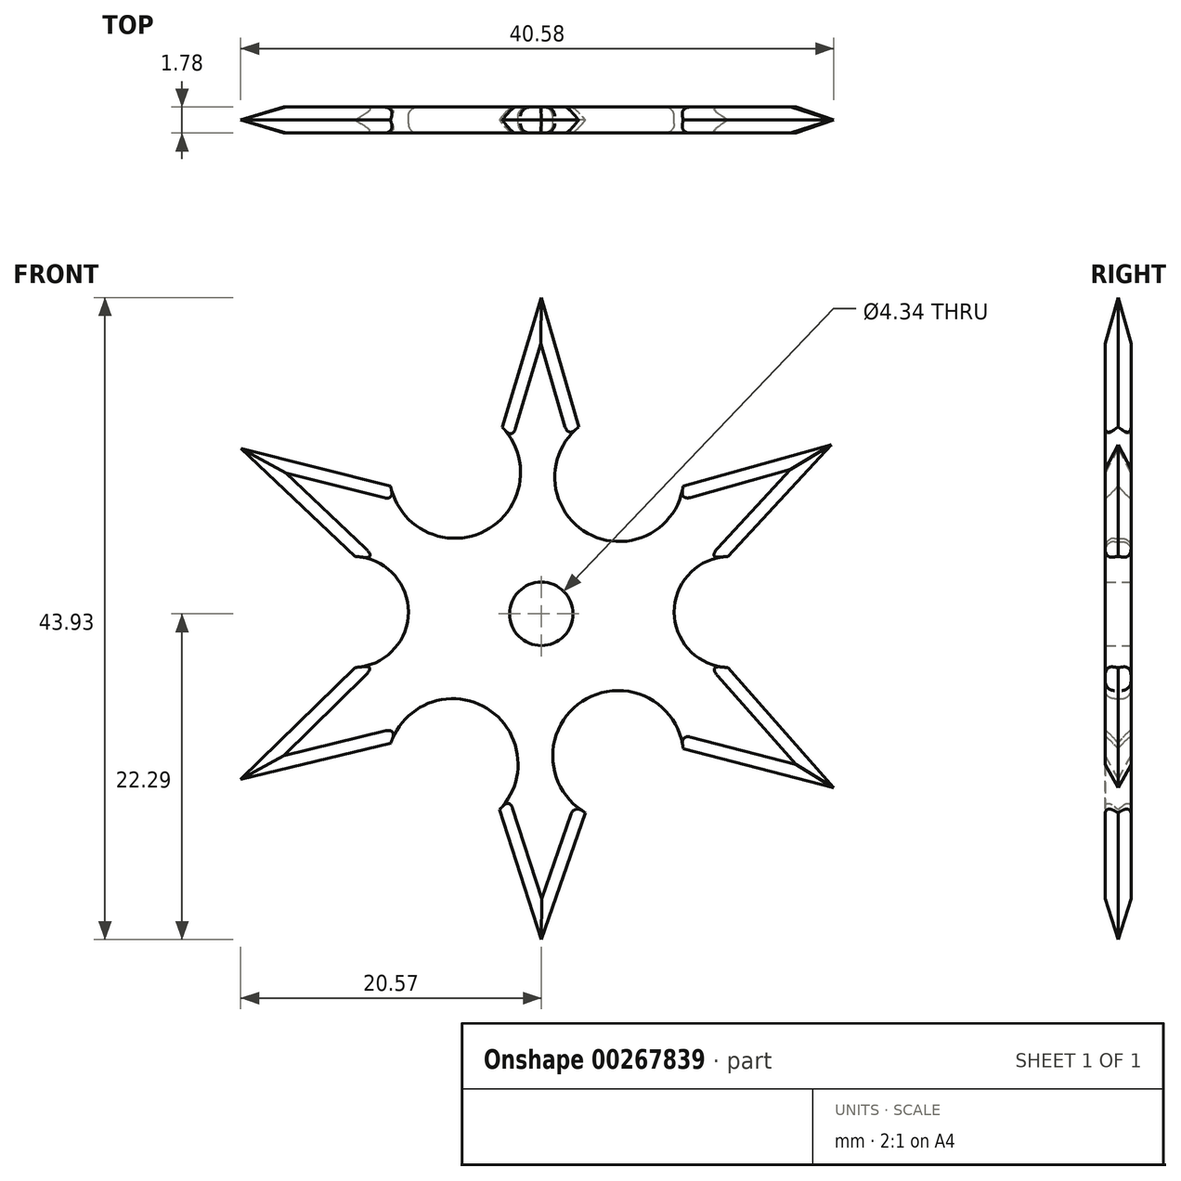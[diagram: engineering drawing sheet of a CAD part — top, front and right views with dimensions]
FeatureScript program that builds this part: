
annotation { "Feature Type Name" : "Feature", "Feature Type Description" : "" }
export const myFeature = defineFeature(function(context is Context, id is Id, definition is map)
    precondition{}
    {
        {
            var Q0;
            Q0=qCreatedBy(makeId("Front.planeOp"),FACE);
            var sketch = newSketch(context, id + "F0", { "sketchPlane" : qUnion([Q0])});
            skCircle(sketch, "E0", {"center": v(0, 0) * mm, "radius": 4.02 * mm});
            skArc(sketch, "E1", {"start": v(-12.92, -3.67) * mm, "mid": v(-9.1, 0.13) * mm, "end": v(-12.92, 3.93) * mm});
            skArc(sketch, "E2", {"start": v(12.92, 3.93) * mm, "mid": v(9.1, 0.13) * mm, "end": v(12.92, -3.67) * mm});
            skPoint(sketch, "E3.startSnap0", {"position": v(-9.1, 0.13) * mm});
            skLineSegment(sketch, "E4", {"start": v(-12.92, -3.67) * mm, "end": v(-20.98, -11.56) * mm});
            skLineSegment(sketch, "E5", {"start": v(-20.98, -11.56) * mm, "end": v(-10.34, -8.98) * mm});
            skLineSegment(sketch, "E6", {"start": v(9.72, -9.35) * mm, "end": v(20.38, -12.12) * mm});
            skLineSegment(sketch, "E7", {"start": v(12.92, -3.67) * mm, "end": v(20.38, -12.12) * mm});
            skLineSegment(sketch, "E8", {"start": v(12.92, 3.93) * mm, "end": v(20.25, 11.82) * mm});
            skLineSegment(sketch, "E9", {"start": v(9.72, 8.88) * mm, "end": v(20.25, 11.82) * mm});
            skLineSegment(sketch, "E10", {"start": v(-12.92, 3.93) * mm, "end": v(-20.98, 11.55) * mm});
            skLineSegment(sketch, "E11", {"start": v(-10.34, 8.88) * mm, "end": v(-20.98, 11.55) * mm});
            skCircle(sketch, "E12", {"center": v(0, 0) * mm, "radius": 2.17 * mm});
            skArc(sketch, "E13", {"start": v(-2.96, -13.5) * mm, "mid": v(-3.73, -6.46) * mm, "end": v(-10.34, -8.98) * mm});
            skArc(sketch, "E14", {"start": v(9.72, -9.35) * mm, "mid": v(2.8, -5.98) * mm, "end": v(3.13, -13.66) * mm});
            skLineSegment(sketch, "E15", {"start": v(-2.96, -13.5) * mm, "end": v(0, -22.69) * mm});
            skLineSegment(sketch, "E16", {"start": v(0, -22.69) * mm, "end": v(3.13, -13.66) * mm});
            skArc(sketch, "E17", {"start": v(-10.34, 8.88) * mm, "mid": v(-3.82, 5.69) * mm, "end": v(-2.77, 12.87) * mm});
            skArc(sketch, "E18", {"start": v(2.66, 12.87) * mm, "mid": v(3.16, 5.52) * mm, "end": v(9.72, 8.88) * mm});
            skLineSegment(sketch, "E19", {"start": v(-2.77, 12.87) * mm, "end": v(0, 22.1) * mm});
            skLineSegment(sketch, "E20", {"start": v(0, 22.1) * mm, "end": v(2.66, 12.87) * mm});
            skLineSegment(sketch, "E21", {"start": v(-2.77, 12.87) * mm, "end": v(2.66, 12.87) * mm});
            skLineSegment(sketch, "E22", {"start": v(-2.96, -13.5) * mm, "end": v(3.13, -13.66) * mm});
            skLineSegment(sketch, "E23", {"start": v(-12.92, -3.67) * mm, "end": v(-10.34, -8.98) * mm});
            skLineSegment(sketch, "E24", {"start": v(-12.92, 3.93) * mm, "end": v(-10.34, 8.88) * mm});
            skLineSegment(sketch, "E25", {"start": v(9.72, 8.88) * mm, "end": v(12.92, 3.93) * mm});
            skLineSegment(sketch, "E26", {"start": v(12.92, -3.67) * mm, "end": v(9.72, -9.35) * mm});
            skPoint(sketch, "E27.endSnap0", {"position": v(-11.63, 6.4) * mm});
            skLineSegment(sketch, "E28", {"start": v(-11.63, 6.4) * mm, "end": v(-20.98, 11.55) * mm});
            skLineSegment(sketch, "E29", {"start": v(0, 22.1) * mm, "end": v(0, 12.87) * mm});
            skLineSegment(sketch, "E30", {"start": v(20.25, 11.82) * mm, "end": v(11.32, 6.4) * mm});
            skLineSegment(sketch, "E31", {"start": v(20.38, -12.12) * mm, "end": v(11.32, -6.51) * mm});
            skLineSegment(sketch, "E32", {"start": v(0, -22.69) * mm, "end": v(0, -13.58) * mm});
            skLineSegment(sketch, "E33", {"start": v(-20.98, -11.56) * mm, "end": v(-11.63, -6.32) * mm});
            skLineSegment(sketch, "E34", {"start": v(-12.92, 3.93) * mm, "end": v(-16.3, 8.98) * mm});
            skLineSegment(sketch, "E35", {"start": v(-16.3, 8.98) * mm, "end": v(-10.34, 8.88) * mm});
            skLineSegment(sketch, "E36", {"start": v(-10.34, -8.98) * mm, "end": v(-16.38, -8.98) * mm});
            skLineSegment(sketch, "E37", {"start": v(-16.38, -8.98) * mm, "end": v(-12.92, -3.67) * mm});
            skLineSegment(sketch, "E38", {"start": v(-2.96, -13.5) * mm, "end": v(0, -18.8) * mm});
            skLineSegment(sketch, "E39", {"start": v(0, -18.8) * mm, "end": v(3.13, -13.66) * mm});
            skLineSegment(sketch, "E40", {"start": v(9.72, -9.35) * mm, "end": v(16.19, -9.53) * mm});
            skLineSegment(sketch, "E41", {"start": v(16.19, -9.53) * mm, "end": v(12.92, -3.67) * mm});
            skLineSegment(sketch, "E42", {"start": v(-2.77, 12.87) * mm, "end": v(0, 17.48) * mm});
            skLineSegment(sketch, "E43", {"start": v(0, 17.48) * mm, "end": v(2.66, 12.87) * mm});
            skPoint(sketch, "E44.endSnap0", {"position": v(15.78, 9.11) * mm});
            skLineSegment(sketch, "E45", {"start": v(9.72, 8.88) * mm, "end": v(15.78, 9.11) * mm});
            skLineSegment(sketch, "E46", {"start": v(15.78, 9.11) * mm, "end": v(12.92, 3.93) * mm});
            skSolve(sketch);
        }
        {
            var Q0;
            Q0=makeQuery(id+"F0.imprint","IMPRINT",FACE,{"disambiguationData":[TD([[makeQuery(id+"F0.imprint","IMPRINT",EDGE,{"derivedFrom":sQuery(id+"F0.wireOp",EDGE,"E0")}),-1.0]])]});
            var Q1;
            Q1=makeQuery(id+"F0.imprint","IMPRINT",FACE,{"disambiguationData":[TD([[makeQuery(id+"F0.imprint","IMPRINT",EDGE,{"derivedFrom":sQuery(id+"F0.wireOp",EDGE,"E0")}),1.0]])]});
            extrude(context, id + "F1", {"entities" : qUnion([Q0, Q1]), "endBound" : BoundingType.SYMMETRIC, "depth" : 1.78 * mm});
        }
        {
            var Q0;
            {var subQ0=sQuery(id+"F0.wireOp",EDGE,"E35");Q0=makeQuery(id+"F0.imprint","IMPRINT",FACE,{"disambiguationData":[TD([[makeQuery(id+"F0.imprint","IMPRINT",EDGE,{"derivedFrom":subQ0}),-1.0]])]});}
            var Q1;
            {var subQ0=sQuery(id+"F0.wireOp",EDGE,"E34");Q1=makeQuery(id+"F0.imprint","IMPRINT",FACE,{"disambiguationData":[TD([[makeQuery(id+"F0.imprint","IMPRINT",EDGE,{"derivedFrom":subQ0}),-1.0]])]});}
            var Q2;
            {var subQ0=sQuery(id+"F0.wireOp",EDGE,"E10");Q2=makeQuery(id+"F0.imprint","IMPRINT",FACE,{"disambiguationData":[TD([[makeQuery(id+"F0.imprint","IMPRINT",EDGE,{"derivedFrom":subQ0}),-1.0]])]});}
            var Q3;
            {var subQ0=sQuery(id+"F0.wireOp",EDGE,"E11");Q3=makeQuery(id+"F0.imprint","IMPRINT",FACE,{"disambiguationData":[TD([[makeQuery(id+"F0.imprint","IMPRINT",EDGE,{"derivedFrom":subQ0}),1.0]])]});}
            var Q4;
            {var subQ0=sQuery(id+"F0.wireOp",EDGE,"E42");Q4=makeQuery(id+"F0.imprint","IMPRINT",FACE,{"disambiguationData":[TD([[makeQuery(id+"F0.imprint","IMPRINT",EDGE,{"derivedFrom":subQ0}),-1.0]])]});}
            var Q5;
            {var subQ0=sQuery(id+"F0.wireOp",EDGE,"E43");Q5=makeQuery(id+"F0.imprint","IMPRINT",FACE,{"disambiguationData":[TD([[makeQuery(id+"F0.imprint","IMPRINT",EDGE,{"derivedFrom":subQ0}),-1.0]])]});}
            var Q6;
            {var subQ0=sQuery(id+"F0.wireOp",EDGE,"E20");Q6=makeQuery(id+"F0.imprint","IMPRINT",FACE,{"disambiguationData":[TD([[makeQuery(id+"F0.imprint","IMPRINT",EDGE,{"derivedFrom":subQ0}),-1.0]])]});}
            var Q7;
            {var subQ0=sQuery(id+"F0.wireOp",EDGE,"E19");Q7=makeQuery(id+"F0.imprint","IMPRINT",FACE,{"disambiguationData":[TD([[makeQuery(id+"F0.imprint","IMPRINT",EDGE,{"derivedFrom":subQ0}),-1.0]])]});}
            var Q8;
            {var subQ0=sQuery(id+"F0.wireOp",EDGE,"E5");Q8=makeQuery(id+"F0.imprint","IMPRINT",FACE,{"disambiguationData":[TD([[makeQuery(id+"F0.imprint","IMPRINT",EDGE,{"derivedFrom":subQ0}),1.0]])]});}
            var Q9;
            {var subQ0=sQuery(id+"F0.wireOp",EDGE,"E4");Q9=makeQuery(id+"F0.imprint","IMPRINT",FACE,{"disambiguationData":[TD([[makeQuery(id+"F0.imprint","IMPRINT",EDGE,{"derivedFrom":subQ0}),1.0]])]});}
            var Q10;
            {var subQ0=sQuery(id+"F0.wireOp",EDGE,"E37");Q10=makeQuery(id+"F0.imprint","IMPRINT",FACE,{"disambiguationData":[TD([[makeQuery(id+"F0.imprint","IMPRINT",EDGE,{"derivedFrom":subQ0}),-1.0]])]});}
            var Q11;
            {var subQ0=sQuery(id+"F0.wireOp",EDGE,"E36");Q11=makeQuery(id+"F0.imprint","IMPRINT",FACE,{"disambiguationData":[TD([[makeQuery(id+"F0.imprint","IMPRINT",EDGE,{"derivedFrom":subQ0}),-1.0]])]});}
            var Q12;
            {var subQ0=sQuery(id+"F0.wireOp",EDGE,"E15");Q12=makeQuery(id+"F0.imprint","IMPRINT",FACE,{"disambiguationData":[TD([[makeQuery(id+"F0.imprint","IMPRINT",EDGE,{"derivedFrom":subQ0}),1.0]])]});}
            var Q13;
            {var subQ0=sQuery(id+"F0.wireOp",EDGE,"E16");Q13=makeQuery(id+"F0.imprint","IMPRINT",FACE,{"disambiguationData":[TD([[makeQuery(id+"F0.imprint","IMPRINT",EDGE,{"derivedFrom":subQ0}),1.0]])]});}
            var Q14;
            {var subQ0=sQuery(id+"F0.wireOp",EDGE,"E39");Q14=makeQuery(id+"F0.imprint","IMPRINT",FACE,{"disambiguationData":[TD([[makeQuery(id+"F0.imprint","IMPRINT",EDGE,{"derivedFrom":subQ0}),1.0]])]});}
            var Q15;
            {var subQ0=sQuery(id+"F0.wireOp",EDGE,"E38");Q15=makeQuery(id+"F0.imprint","IMPRINT",FACE,{"disambiguationData":[TD([[makeQuery(id+"F0.imprint","IMPRINT",EDGE,{"derivedFrom":subQ0}),1.0]])]});}
            var Q16;
            {var subQ0=sQuery(id+"F0.wireOp",EDGE,"E7");Q16=makeQuery(id+"F0.imprint","IMPRINT",FACE,{"disambiguationData":[TD([[makeQuery(id+"F0.imprint","IMPRINT",EDGE,{"derivedFrom":subQ0}),-1.0]])]});}
            var Q17;
            {var subQ0=sQuery(id+"F0.wireOp",EDGE,"E41");Q17=makeQuery(id+"F0.imprint","IMPRINT",FACE,{"disambiguationData":[TD([[makeQuery(id+"F0.imprint","IMPRINT",EDGE,{"derivedFrom":subQ0}),1.0]])]});}
            var Q18;
            {var subQ0=sQuery(id+"F0.wireOp",EDGE,"E40");Q18=makeQuery(id+"F0.imprint","IMPRINT",FACE,{"disambiguationData":[TD([[makeQuery(id+"F0.imprint","IMPRINT",EDGE,{"derivedFrom":subQ0}),1.0]])]});}
            var Q19;
            {var subQ0=sQuery(id+"F0.wireOp",EDGE,"E6");Q19=makeQuery(id+"F0.imprint","IMPRINT",FACE,{"disambiguationData":[TD([[makeQuery(id+"F0.imprint","IMPRINT",EDGE,{"derivedFrom":subQ0}),1.0]])]});}
            var Q20;
            {var subQ0=sQuery(id+"F0.wireOp",EDGE,"E8");Q20=makeQuery(id+"F0.imprint","IMPRINT",FACE,{"disambiguationData":[TD([[makeQuery(id+"F0.imprint","IMPRINT",EDGE,{"derivedFrom":subQ0}),1.0]])]});}
            var Q21;
            {var subQ0=sQuery(id+"F0.wireOp",EDGE,"E9");Q21=makeQuery(id+"F0.imprint","IMPRINT",FACE,{"disambiguationData":[TD([[makeQuery(id+"F0.imprint","IMPRINT",EDGE,{"derivedFrom":subQ0}),-1.0]])]});}
            var Q22;
            {var subQ0=sQuery(id+"F0.wireOp",EDGE,"E45");Q22=makeQuery(id+"F0.imprint","IMPRINT",FACE,{"disambiguationData":[TD([[makeQuery(id+"F0.imprint","IMPRINT",EDGE,{"derivedFrom":subQ0}),-1.0]])]});}
            var Q23;
            {var subQ0=sQuery(id+"F0.wireOp",EDGE,"E46");Q23=makeQuery(id+"F0.imprint","IMPRINT",FACE,{"disambiguationData":[TD([[makeQuery(id+"F0.imprint","IMPRINT",EDGE,{"derivedFrom":subQ0}),-1.0]])]});}
            extrude(context, id + "F2", {"entities" : qUnion([Q0, Q1, Q2, Q3, Q4, Q5, Q6, Q7, Q8, Q9, Q10, Q11, Q12, Q13, Q14, Q15, Q16, Q17, Q18, Q19, Q20, Q21, Q22, Q23]), "operationType" : NewBodyOperationType.ADD, "endBound" : BoundingType.SYMMETRIC, "depth" : 1.78 * mm});
        }
        {
            var Q0;
            Q0=makeQuery(id+"F2.opExtrude","CAP_EDGE",EDGE,{"disambiguationData":[OSD([sQuery(id+"F0.wireOp",EDGE,"E11")])],"isStart":false});
            var Q1;
            Q1=makeQuery(id+"F2.opExtrude","CAP_EDGE",EDGE,{"disambiguationData":[OSD([sQuery(id+"F0.wireOp",EDGE,"E10")])],"isStart":false});
            var Q2;
            Q2=makeQuery(id+"F2.opExtrude","CAP_EDGE",EDGE,{"disambiguationData":[OSD([sQuery(id+"F0.wireOp",EDGE,"E19")])],"isStart":false});
            var Q3;
            Q3=makeQuery(id+"F2.opExtrude","CAP_EDGE",EDGE,{"disambiguationData":[OSD([sQuery(id+"F0.wireOp",EDGE,"E20")])],"isStart":false});
            var Q4;
            Q4=makeQuery(id+"F2.opExtrude","CAP_EDGE",EDGE,{"disambiguationData":[OSD([sQuery(id+"F0.wireOp",EDGE,"E9")])],"isStart":false});
            var Q5;
            Q5=makeQuery(id+"F2.opExtrude","CAP_EDGE",EDGE,{"disambiguationData":[OSD([sQuery(id+"F0.wireOp",EDGE,"E8")])],"isStart":false});
            var Q6;
            Q6=makeQuery(id+"F2.opExtrude","CAP_EDGE",EDGE,{"disambiguationData":[OSD([sQuery(id+"F0.wireOp",EDGE,"E7")])],"isStart":false});
            var Q7;
            Q7=makeQuery(id+"F2.opExtrude","CAP_EDGE",EDGE,{"disambiguationData":[OSD([sQuery(id+"F0.wireOp",EDGE,"E6")])],"isStart":false});
            var Q8;
            Q8=makeQuery(id+"F2.opExtrude","CAP_EDGE",EDGE,{"disambiguationData":[OSD([sQuery(id+"F0.wireOp",EDGE,"E16")])],"isStart":false});
            var Q9;
            Q9=makeQuery(id+"F2.opExtrude","CAP_EDGE",EDGE,{"disambiguationData":[OSD([sQuery(id+"F0.wireOp",EDGE,"E15")])],"isStart":false});
            var Q10;
            Q10=makeQuery(id+"F2.opExtrude","CAP_EDGE",EDGE,{"disambiguationData":[OSD([sQuery(id+"F0.wireOp",EDGE,"E5")])],"isStart":false});
            var Q11;
            Q11=makeQuery(id+"F2.opExtrude","CAP_EDGE",EDGE,{"disambiguationData":[OSD([sQuery(id+"F0.wireOp",EDGE,"E4")])],"isStart":false});
            chamfer(context, id + "F3", {"entities" : qUnion([Q0, Q1, Q2, Q3, Q4, Q5, Q6, Q7, Q8, Q9, Q10, Q11]), "width" : 1.02 * mm, "tangentPropagation" : true});
        }
        {
            var Q0;
            Q0=makeQuery(id+"F1.opExtrude","CAP_EDGE",EDGE,{"disambiguationData":[OSD([sQuery(id+"F0.wireOp",EDGE,"E13")])],"isStart":false});
            var Q1;
            Q1=makeQuery(id+"F1.opExtrude","CAP_EDGE",EDGE,{"disambiguationData":[OSD([sQuery(id+"F0.wireOp",EDGE,"E14")])],"isStart":false});
            var Q2;
            Q2=makeQuery(id+"F1.opExtrude","CAP_EDGE",EDGE,{"disambiguationData":[OSD([sQuery(id+"F0.wireOp",EDGE,"E2")])],"isStart":false});
            var Q3;
            Q3=makeQuery(id+"F1.opExtrude","CAP_EDGE",EDGE,{"disambiguationData":[OSD([sQuery(id+"F0.wireOp",EDGE,"E18")])],"isStart":false});
            var Q4;
            Q4=makeQuery(id+"F1.opExtrude","CAP_EDGE",EDGE,{"disambiguationData":[OSD([sQuery(id+"F0.wireOp",EDGE,"E17")])],"isStart":false});
            var Q5;
            Q5=makeQuery(id+"F1.opExtrude","CAP_EDGE",EDGE,{"disambiguationData":[OSD([sQuery(id+"F0.wireOp",EDGE,"E1")])],"isStart":false});
            fillet(context, id + "F4", {"entities" : qUnion([Q0, Q1, Q2, Q3, Q4, Q5]), "radius" : 0.64 * mm, "tangentPropagation" : true, "allowEdgeOverflow" : false});
        }
        {
            var Q0;
            Q0=makeQuery(id+"F2.opExtrude","CAP_EDGE",EDGE,{"disambiguationData":[OSD([sQuery(id+"F0.wireOp",EDGE,"E8")])],"isStart":true});
            var Q1;
            Q1=makeQuery(id+"F2.opExtrude","CAP_EDGE",EDGE,{"disambiguationData":[OSD([sQuery(id+"F0.wireOp",EDGE,"E9")])],"isStart":true});
            var Q2;
            Q2=makeQuery(id+"F2.opExtrude","CAP_EDGE",EDGE,{"disambiguationData":[OSD([sQuery(id+"F0.wireOp",EDGE,"E11")])],"isStart":true});
            var Q3;
            Q3=makeQuery(id+"F2.opExtrude","CAP_EDGE",EDGE,{"disambiguationData":[OSD([sQuery(id+"F0.wireOp",EDGE,"E10")])],"isStart":true});
            var Q4;
            Q4=makeQuery(id+"F2.opExtrude","CAP_EDGE",EDGE,{"disambiguationData":[OSD([sQuery(id+"F0.wireOp",EDGE,"E4")])],"isStart":true});
            var Q5;
            Q5=makeQuery(id+"F2.opExtrude","CAP_EDGE",EDGE,{"disambiguationData":[OSD([sQuery(id+"F0.wireOp",EDGE,"E5")])],"isStart":true});
            var Q6;
            Q6=makeQuery(id+"F2.opExtrude","CAP_EDGE",EDGE,{"disambiguationData":[OSD([sQuery(id+"F0.wireOp",EDGE,"E15")])],"isStart":true});
            var Q7;
            Q7=makeQuery(id+"F2.opExtrude","CAP_EDGE",EDGE,{"disambiguationData":[OSD([sQuery(id+"F0.wireOp",EDGE,"E16")])],"isStart":true});
            var Q8;
            Q8=makeQuery(id+"F2.opExtrude","CAP_EDGE",EDGE,{"disambiguationData":[OSD([sQuery(id+"F0.wireOp",EDGE,"E6")])],"isStart":true});
            var Q9;
            Q9=makeQuery(id+"F2.opExtrude","CAP_EDGE",EDGE,{"disambiguationData":[OSD([sQuery(id+"F0.wireOp",EDGE,"E7")])],"isStart":true});
            var Q10;
            Q10=makeQuery(id+"F2.opExtrude","CAP_EDGE",EDGE,{"disambiguationData":[OSD([sQuery(id+"F0.wireOp",EDGE,"E19")])],"isStart":true});
            var Q11;
            Q11=makeQuery(id+"F2.opExtrude","CAP_EDGE",EDGE,{"disambiguationData":[OSD([sQuery(id+"F0.wireOp",EDGE,"E20")])],"isStart":true});
            chamfer(context, id + "F5", {"entities" : qUnion([Q0, Q1, Q2, Q3, Q4, Q5, Q6, Q7, Q8, Q9, Q10, Q11]), "width" : 1.02 * mm, "tangentPropagation" : true});
        }
        {
            var Q0;
            Q0=makeQuery(id+"F1.opExtrude","CAP_EDGE",EDGE,{"disambiguationData":[OSD([sQuery(id+"F0.wireOp",EDGE,"E18")])],"isStart":true});
            var Q1;
            Q1=makeQuery(id+"F1.opExtrude","CAP_EDGE",EDGE,{"disambiguationData":[OSD([sQuery(id+"F0.wireOp",EDGE,"E17")])],"isStart":true});
            var Q2;
            Q2=makeQuery(id+"F1.opExtrude","CAP_EDGE",EDGE,{"disambiguationData":[OSD([sQuery(id+"F0.wireOp",EDGE,"E1")])],"isStart":true});
            var Q3;
            Q3=makeQuery(id+"F1.opExtrude","CAP_EDGE",EDGE,{"disambiguationData":[OSD([sQuery(id+"F0.wireOp",EDGE,"E13")])],"isStart":true});
            var Q4;
            Q4=makeQuery(id+"F1.opExtrude","CAP_EDGE",EDGE,{"disambiguationData":[OSD([sQuery(id+"F0.wireOp",EDGE,"E14")])],"isStart":true});
            var Q5;
            Q5=makeQuery(id+"F1.opExtrude","CAP_EDGE",EDGE,{"disambiguationData":[OSD([sQuery(id+"F0.wireOp",EDGE,"E2")])],"isStart":true});
            fillet(context, id + "F6", {"entities" : qUnion([Q0, Q1, Q2, Q3, Q4, Q5]), "radius" : 0.64 * mm, "tangentPropagation" : true, "allowEdgeOverflow" : false});
        }
    });
